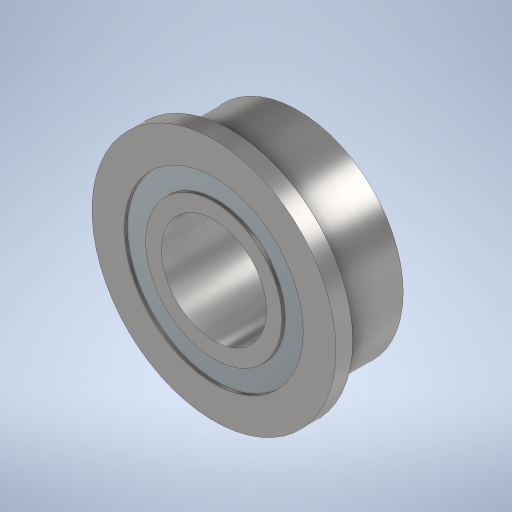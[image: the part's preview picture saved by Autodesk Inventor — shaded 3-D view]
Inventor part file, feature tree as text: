
AUTODESK INVENTOR PART (.ipt)
format: ipt  version: 2024 (Build 280153000, 153)  size: 296,960 bytes
history: native  units: mm
features: extrude x3, sketch x2
ambient origin geometry x8: Origin, YZ Plane, XZ Plane, XY Plane, X Axis, Y Axis, Z Axis, Center Point
bodies: Solid1 (feature_tree)
feature tree (5):
  sketch  "Sketch1"  dims[d0=5.0mm d1=10.0mm]
  extrude  "Extrusion1"  Depth=10.0mm
  extrude  "Extrusion2"  Depth=0.8mm
  extrude  "Extrusion3"  Depth=4.0mm TaperAngle=0.0deg
  sketch  "Sketch2"  dims[d2=0.75mm d3=0.75mm d4=4.0mm d5=0.0mm d6=3.75mm d7=0.0mm d8=11.6mm d9=0.8mm d10=0.0mm]
